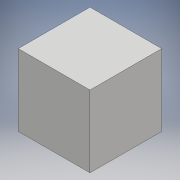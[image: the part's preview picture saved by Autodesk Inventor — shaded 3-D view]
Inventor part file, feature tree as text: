
AUTODESK INVENTOR PART (.ipt)
format: ipt  version: 2018 (Build 220112000, 112)  size: 84,480 bytes
history: native  units: mm
features: extrude x1, sketch x1
ambient origin geometry x8: Origin, YZ Plane, XZ Plane, XY Plane, X Axis, Y Axis, Z Axis, Center Point
bodies: Solid1 (feature_tree)
feature tree (2):
  extrude  "Extrusion1"  Depth=12.0mm
  sketch  "Sketch1"  dims[d0=12.0mm d1=12.0mm d2=12.0mm d3=0.0mm]
